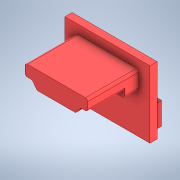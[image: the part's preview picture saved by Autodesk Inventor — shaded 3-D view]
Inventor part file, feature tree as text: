
AUTODESK INVENTOR PART (.ipt)
format: ipt  version: 2021 (Build 250183000, 183)  size: 163,840 bytes
history: native  units: mm
features: extrude x4, sketch x4, plane x1, fillet x1, projected_geometry x1
ambient origin geometry x8: Origin, YZ Plane, XZ Plane, XY Plane, X Axis, Y Axis, Z Axis, Center Point
bodies: Solid1 (feature_tree)
feature tree (11):
  extrude  "Extrusion1"  Depth=15.0mm
  extrude  "Extrusion2"  Depth=5.0mm
  sketch  "Sketch3"  dims[d5=1.0mm d6=17.0mm]
  plane  "Work Plane1"
  extrude  "Extrusion3"  Depth=17.0mm
  extrude  "Extrusion4"  Depth=14.0mm
  fillet  "Fillet1"  Radius=4.0mm
  sketch  "Sketch1"  dims[d0=19.0mm d1=15.0mm]
  sketch  "Sketch2"  dims[d2=1.6mm d3=0.0mm d4=5.0mm]
  sketch  "Sketch4"  dims[d7=2.0mm d8=0.0mm d9=14.0mm d10=4.0mm d11=2.0mm d12=-15.0mm d13=2.0mm d14=0.0mm d15=8.25mm d16=0.0mm d17=0.5mm]
  projected_geometry  "Projected Loop1"
